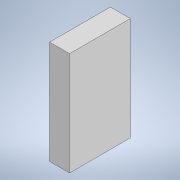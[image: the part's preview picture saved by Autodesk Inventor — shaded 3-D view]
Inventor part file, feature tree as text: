
AUTODESK INVENTOR PART (.ipt)
format: ipt  version: 2022.3 (Build 263350000, 350)  size: 89,088 bytes
history: native  units: in
note: dims shown in document units (in); Inventor stores cm internally (conversion verified against a paired STEP export)
features: extrude x1, sketch x1
ambient origin geometry x8: Origin, YZ Plane, XZ Plane, XY Plane, X Axis, Y Axis, Z Axis, Center Point
bodies: Solid1 (feature_tree)
feature tree (2):
  extrude  "Extrusion1"  Depth=1.1in
  sketch  "Sketch1"  dims[d0=3.35in d1=1.1in d2=5.7in d3=0.0in]
